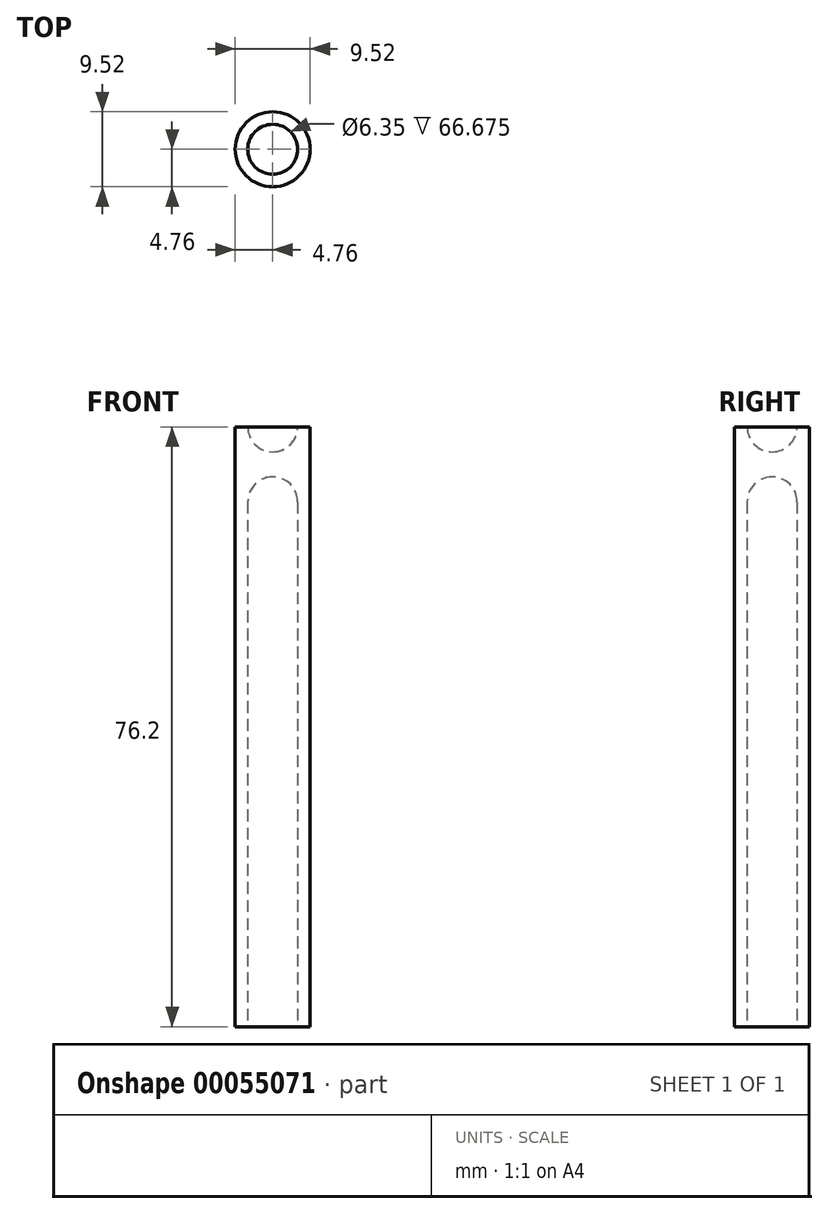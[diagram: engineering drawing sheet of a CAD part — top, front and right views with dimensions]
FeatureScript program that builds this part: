
annotation { "Feature Type Name" : "Feature", "Feature Type Description" : "" }
export const myFeature = defineFeature(function(context is Context, id is Id, definition is map)
    precondition{}
    {
        {
            var Q0;
            Q0=qCreatedBy(makeId("Top.planeOp"),FACE);
            var sketch = newSketch(context, id + "F0", { "sketchPlane" : qUnion([Q0])});
            skCircle(sketch, "E0", {"center": v(0, 0) * mm, "radius": 4.76 * mm});
            skSolve(sketch);
        }
        {
            var Q0;
            Q0=makeQuery(id+"F0.imprint","IMPRINT",FACE,{"disambiguationData":[TD([[makeQuery(id+"F0.imprint","IMPRINT",EDGE,{"derivedFrom":sQuery(id+"F0.wireOp",EDGE,"E0")}),1.0]])]});
            extrude(context, id + "F1", {"entities" : qUnion([Q0]), "depth" : 76.2 * mm});
        }
        {
            var Q0;
            Q0=makeQuery(id+"F1.opExtrude","CAP_FACE",FACE,{"disambiguationData":[OSD([sQuery(id+"F0.wireOp",EDGE,"E0")])],"isStart":false});
            var sketch = newSketch(context, id + "F2", { "sketchPlane" : qUnion([Q0])});
            skCircle(sketch, "E1", {"center": v(0, 0) * mm, "radius": 3.18 * mm});
            skSolve(sketch);
        }
        {
            var Q0;
            Q0=makeQuery(id+"F2.imprint","IMPRINT",FACE,{"disambiguationData":[TD([[makeQuery(id+"F2.imprint","IMPRINT",EDGE,{"derivedFrom":sQuery(id+"F2.wireOp",EDGE,"E1")}),1.0]])]});
            extrude(context, id + "F3", {"entities" : qUnion([Q0]), "operationType" : NewBodyOperationType.REMOVE, "oppositeDirection" : true, "depth" : 3.17 * mm});
        }
        {
            var Q0;
            Q0=makeQuery(id+"F3.boolean.opBoolean","COPY",EDGE,{"derivedFrom":makeQuery(id+"F3.opExtrude","CAP_EDGE",EDGE,{"disambiguationData":[OSD([sQuery(id+"F2.wireOp",EDGE,"E1")])],"isStart":false})});
            fillet(context, id + "F4", {"entities" : qUnion([Q0]), "radius" : 3.17 * mm, "tangentPropagation" : true, "allowEdgeOverflow" : false});
        }
        {
            var Q0;
            Q0=makeQuery(id+"F1.opExtrude","CAP_FACE",FACE,{"disambiguationData":[OSD([sQuery(id+"F0.wireOp",EDGE,"E0")])],"isStart":true});
            var sketch = newSketch(context, id + "F5", { "sketchPlane" : qUnion([Q0])});
            skCircle(sketch, "E2", {"center": v(0, 0) * mm, "radius": 3.18 * mm});
            skSolve(sketch);
        }
        {
            var Q0;
            Q0=makeQuery(id+"F5.imprint","IMPRINT",FACE,{"disambiguationData":[TD([[makeQuery(id+"F5.imprint","IMPRINT",EDGE,{"derivedFrom":sQuery(id+"F5.wireOp",EDGE,"E2")}),1.0]])]});
            extrude(context, id + "F6", {"entities" : qUnion([Q0]), "operationType" : NewBodyOperationType.REMOVE, "oppositeDirection" : true, "depth" : 69.85 * mm});
        }
        {
            var Q0;
            Q0=makeQuery(id+"F6.boolean.opBoolean","COPY",EDGE,{"derivedFrom":makeQuery(id+"F6.opExtrude","CAP_EDGE",EDGE,{"disambiguationData":[OSD([sQuery(id+"F5.wireOp",EDGE,"E2")])],"isStart":false})});
            fillet(context, id + "F7", {"entities" : qUnion([Q0]), "radius" : 3.17 * mm, "tangentPropagation" : true, "allowEdgeOverflow" : false});
        }
    });
